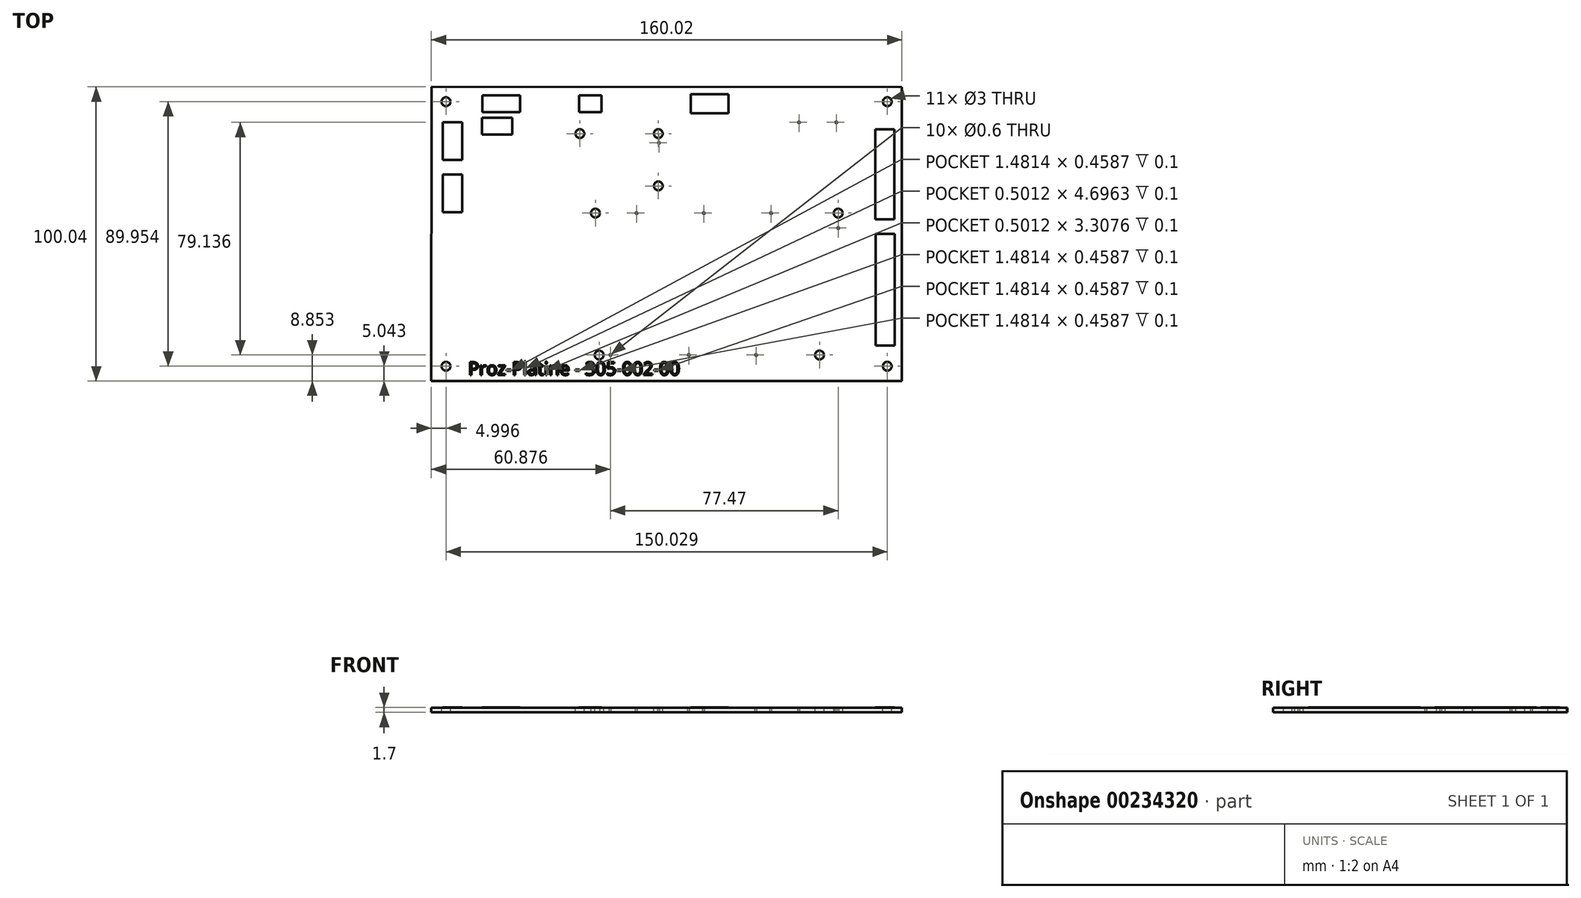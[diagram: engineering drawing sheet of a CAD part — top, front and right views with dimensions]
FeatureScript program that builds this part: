
annotation { "Feature Type Name" : "Feature", "Feature Type Description" : "" }
export const myFeature = defineFeature(function(context is Context, id is Id, definition is map)
    precondition{}
    {
        {
            var Q0;
            Q0=qCreatedBy(makeId("Top.planeOp"),FACE);
            var sketch = newSketch(context, id + "F0", { "sketchPlane" : qUnion([Q0])});
            skLineSegment(sketch, "E0.bottom", {"start": v(79.99, -50.02) * mm, "end": v(-80.01, -49.98) * mm});
            skLineSegment(sketch, "E0.top", {"start": v(80.01, 49.98) * mm, "end": v(-79.99, 50.02) * mm});
            skLineSegment(sketch, "E0.left", {"start": v(79.99, -50.02) * mm, "end": v(80.01, 49.98) * mm});
            skLineSegment(sketch, "E0.right", {"start": v(-80.01, -49.98) * mm, "end": v(-79.99, 50.02) * mm});
            skPoint(sketch, "E0.middle", {"position": v(0, 0) * mm});
            skCircle(sketch, "E1", {"center": v(-75.01, -44.98) * mm, "radius": 1.5 * mm});
            skCircle(sketch, "E2.MirrorC", {"center": v(75.01, -44.98) * mm, "radius": 1.5 * mm});
            skCircle(sketch, "E3.MirrorC", {"center": v(-75.01, 44.98) * mm, "radius": 1.5 * mm});
            skCircle(sketch, "E4.MirrorC", {"center": v(75.01, 44.98) * mm, "radius": 1.5 * mm});
            skCircle(sketch, "E5", {"center": v(-22.94, -41.17) * mm, "radius": 1.5 * mm});
            skCircle(sketch, "E6", {"center": v(-24.21, 7.1) * mm, "radius": 1.5 * mm});
            skCircle(sketch, "E7", {"center": v(58.34, 7.1) * mm, "radius": 1.5 * mm});
            skCircle(sketch, "E8", {"center": v(51.99, -41.17) * mm, "radius": 1.5 * mm});
            skCircle(sketch, "E9", {"center": v(-29.5, 34.12) * mm, "radius": 1.5 * mm});
            skCircle(sketch, "E10", {"center": v(-2.83, 34.12) * mm, "radius": 1.5 * mm});
            skCircle(sketch, "E11", {"center": v(-2.83, 16.34) * mm, "radius": 1.5 * mm});
            skCircle(sketch, "E12", {"center": v(-19.13, -41.17) * mm, "radius": 0.3 * mm});
            skCircle(sketch, "E13", {"center": v(7.54, -41.17) * mm, "radius": 0.3 * mm});
            skCircle(sketch, "E14", {"center": v(30.4, -41.17) * mm, "radius": 0.3 * mm});
            skCircle(sketch, "E15", {"center": v(58.34, 2.01) * mm, "radius": 0.3 * mm});
            skCircle(sketch, "E16", {"center": v(-10.24, 7.1) * mm, "radius": 0.3 * mm});
            skCircle(sketch, "E17", {"center": v(12.62, 7.1) * mm, "radius": 0.3 * mm});
            skCircle(sketch, "E18", {"center": v(35.48, 7.1) * mm, "radius": 0.3 * mm});
            skCircle(sketch, "E19", {"center": v(57.7, 37.97) * mm, "radius": 0.3 * mm});
            skCircle(sketch, "E20", {"center": v(45, 37.97) * mm, "radius": 0.3 * mm});
            skCircle(sketch, "E21", {"center": v(-2.62, 31) * mm, "radius": 0.3 * mm});
            skLineSegment(sketch, "E22.bottom", {"start": v(-69.58, 25.22) * mm, "end": v(-76.08, 25.22) * mm});
            skLineSegment(sketch, "E22.top", {"start": v(-69.58, 38.02) * mm, "end": v(-76.08, 38.02) * mm});
            skLineSegment(sketch, "E22.left", {"start": v(-69.58, 25.22) * mm, "end": v(-69.58, 38.02) * mm});
            skLineSegment(sketch, "E22.right", {"start": v(-76.08, 25.22) * mm, "end": v(-76.08, 38.02) * mm});
            skPoint(sketch, "E22.middle", {"position": v(-72.83, 31.62) * mm});
            skLineSegment(sketch, "E23.bottom", {"start": v(-69.58, 7.44) * mm, "end": v(-76.08, 7.44) * mm});
            skLineSegment(sketch, "E23.top", {"start": v(-69.58, 20.24) * mm, "end": v(-76.08, 20.24) * mm});
            skLineSegment(sketch, "E23.left", {"start": v(-69.58, 7.44) * mm, "end": v(-69.58, 20.24) * mm});
            skLineSegment(sketch, "E23.right", {"start": v(-76.08, 7.44) * mm, "end": v(-76.08, 20.24) * mm});
            skPoint(sketch, "E23.middle", {"position": v(-72.83, 13.84) * mm});
            skLineSegment(sketch, "E24.bottom", {"start": v(21, 41.05) * mm, "end": v(8.2, 41.05) * mm});
            skLineSegment(sketch, "E24.top", {"start": v(21, 47.55) * mm, "end": v(8.2, 47.55) * mm});
            skLineSegment(sketch, "E24.left", {"start": v(21, 41.05) * mm, "end": v(21, 47.55) * mm});
            skLineSegment(sketch, "E24.right", {"start": v(8.2, 41.05) * mm, "end": v(8.2, 47.55) * mm});
            skPoint(sketch, "E24.middle", {"position": v(14.6, 44.3) * mm});
            skLineSegment(sketch, "E25.bottom", {"start": v(77.39, 4.99) * mm, "end": v(70.89, 4.99) * mm});
            skLineSegment(sketch, "E25.top", {"start": v(77.39, 35.59) * mm, "end": v(70.89, 35.59) * mm});
            skLineSegment(sketch, "E25.left", {"start": v(77.39, 4.99) * mm, "end": v(77.39, 35.59) * mm});
            skLineSegment(sketch, "E25.right", {"start": v(70.89, 4.99) * mm, "end": v(70.89, 35.59) * mm});
            skPoint(sketch, "E25.middle", {"position": v(74.14, 20.29) * mm});
            skLineSegment(sketch, "E26.bottom", {"start": v(77.56, -37.95) * mm, "end": v(71.06, -37.95) * mm});
            skLineSegment(sketch, "E26.top", {"start": v(77.56, 0.05) * mm, "end": v(71.06, 0.05) * mm});
            skLineSegment(sketch, "E26.left", {"start": v(77.56, -37.95) * mm, "end": v(77.56, 0.05) * mm});
            skLineSegment(sketch, "E26.right", {"start": v(71.06, -37.95) * mm, "end": v(71.06, 0.05) * mm});
            skPoint(sketch, "E26.middle", {"position": v(74.3, -18.95) * mm});
            skLineSegment(sketch, "E27.bottom", {"start": v(-49.9, 41.47) * mm, "end": v(-62.7, 41.47) * mm});
            skLineSegment(sketch, "E27.top", {"start": v(-49.9, 47.17) * mm, "end": v(-62.7, 47.17) * mm});
            skLineSegment(sketch, "E27.left", {"start": v(-49.9, 41.47) * mm, "end": v(-49.9, 47.17) * mm});
            skLineSegment(sketch, "E27.right", {"start": v(-62.7, 41.47) * mm, "end": v(-62.7, 47.17) * mm});
            skPoint(sketch, "E27.middle", {"position": v(-56.3, 44.32) * mm});
            skLineSegment(sketch, "E28.bottom", {"start": v(-52.54, 33.86) * mm, "end": v(-62.84, 33.86) * mm});
            skLineSegment(sketch, "E28.top", {"start": v(-52.54, 39.56) * mm, "end": v(-62.84, 39.56) * mm});
            skLineSegment(sketch, "E28.left", {"start": v(-52.54, 33.86) * mm, "end": v(-52.54, 39.56) * mm});
            skLineSegment(sketch, "E28.right", {"start": v(-62.84, 33.86) * mm, "end": v(-62.84, 39.56) * mm});
            skPoint(sketch, "E28.middle", {"position": v(-57.7, 36.71) * mm});
            skLineSegment(sketch, "E29.bottom", {"start": v(-22.12, 41.4) * mm, "end": v(-29.72, 41.4) * mm});
            skLineSegment(sketch, "E29.top", {"start": v(-22.12, 47.1) * mm, "end": v(-29.72, 47.1) * mm});
            skLineSegment(sketch, "E29.left", {"start": v(-22.12, 41.4) * mm, "end": v(-22.12, 47.1) * mm});
            skLineSegment(sketch, "E29.right", {"start": v(-29.72, 41.4) * mm, "end": v(-29.72, 47.1) * mm});
            skPoint(sketch, "E29.middle", {"position": v(-25.92, 44.26) * mm});
            skSolve(sketch);
        }
        {
            var Q0;
            Q0=makeQuery(id+"F0.imprint","IMPRINT",FACE,{"disambiguationData":[TD([[makeQuery(id+"F0.imprint","IMPRINT",EDGE,{"derivedFrom":sQuery(id+"F0.wireOp",EDGE,"E0.bottom")}),-1.0]])]});
            var Q1;
            Q1=makeQuery(id+"F0.imprint","IMPRINT",FACE,{"disambiguationData":[TD([[makeQuery(id+"F0.imprint","IMPRINT",EDGE,{"derivedFrom":sQuery(id+"F0.wireOp",EDGE,"E23.bottom")}),-1.0]])]});
            var Q2;
            Q2=makeQuery(id+"F0.imprint","IMPRINT",FACE,{"disambiguationData":[TD([[makeQuery(id+"F0.imprint","IMPRINT",EDGE,{"derivedFrom":sQuery(id+"F0.wireOp",EDGE,"E22.bottom")}),-1.0]])]});
            var Q3;
            Q3=makeQuery(id+"F0.imprint","IMPRINT",FACE,{"disambiguationData":[TD([[makeQuery(id+"F0.imprint","IMPRINT",EDGE,{"derivedFrom":sQuery(id+"F0.wireOp",EDGE,"E28.bottom")}),-1.0]])]});
            var Q4;
            Q4=makeQuery(id+"F0.imprint","IMPRINT",FACE,{"disambiguationData":[TD([[makeQuery(id+"F0.imprint","IMPRINT",EDGE,{"derivedFrom":sQuery(id+"F0.wireOp",EDGE,"E27.bottom")}),-1.0]])]});
            var Q5;
            Q5=makeQuery(id+"F0.imprint","IMPRINT",FACE,{"disambiguationData":[TD([[makeQuery(id+"F0.imprint","IMPRINT",EDGE,{"derivedFrom":sQuery(id+"F0.wireOp",EDGE,"E29.bottom")}),-1.0]])]});
            var Q6;
            Q6=makeQuery(id+"F0.imprint","IMPRINT",FACE,{"disambiguationData":[TD([[makeQuery(id+"F0.imprint","IMPRINT",EDGE,{"derivedFrom":sQuery(id+"F0.wireOp",EDGE,"E24.bottom")}),-1.0]])]});
            var Q7;
            Q7=makeQuery(id+"F0.imprint","IMPRINT",FACE,{"disambiguationData":[TD([[makeQuery(id+"F0.imprint","IMPRINT",EDGE,{"derivedFrom":sQuery(id+"F0.wireOp",EDGE,"E25.bottom")}),-1.0]])]});
            var Q8;
            Q8=makeQuery(id+"F0.imprint","IMPRINT",FACE,{"disambiguationData":[TD([[makeQuery(id+"F0.imprint","IMPRINT",EDGE,{"derivedFrom":sQuery(id+"F0.wireOp",EDGE,"E26.bottom")}),-1.0]])]});
            extrude(context, id + "F1", {"entities" : qUnion([Q0, Q1, Q2, Q3, Q4, Q5, Q6, Q7, Q8]), "oppositeDirection" : true, "offsetDistance" : 25 * mm, "depth" : 1.6 * mm});
        }
        {
            var Q0;
            Q0=makeQuery(id+"F1.opExtrude","CAP_FACE",FACE,{"disambiguationData":[OSD([sQuery(id+"F0.wireOp",EDGE,"E0.bottom"),sQuery(id+"F0.wireOp",EDGE,"E0.top"),sQuery(id+"F0.wireOp",EDGE,"E0.left"),sQuery(id+"F0.wireOp",EDGE,"E0.right"),sQuery(id+"F0.wireOp",EDGE,"E1"),sQuery(id+"F0.wireOp",EDGE,"E2.MirrorC")])],"isStart":true});
            var sketch = newSketch(context, id + "F2", { "sketchPlane" : qUnion([Q0])});
            skText(sketch, "E30", { "text": "Proz-Platine - 305-002-00", "fontName": "OpenSans-Regular.ttf"});
            const initialGuessF2  = {"E30": [-0.06752, -0.04799, 1, 0, 0.00445]};
            skSetInitialGuess(sketch, initialGuessF2);
            skSolve(sketch);
        }
        {
            var Q0;
            Q0=qSketchRegion(id+"F2",true);
            extrude(context, id + "F3", {"entities" : qUnion([Q0]), "operationType" : NewBodyOperationType.REMOVE, "oppositeDirection" : true, "depth" : .1 * mm});
        }
        {
            var Q0;
            Q0=makeQuery(id+"F0.imprint","IMPRINT",FACE,{"disambiguationData":[TD([[makeQuery(id+"F0.imprint","IMPRINT",EDGE,{"derivedFrom":sQuery(id+"F0.wireOp",EDGE,"E23.bottom")}),-1.0]])]});
            var Q1;
            Q1=makeQuery(id+"F0.imprint","IMPRINT",FACE,{"disambiguationData":[TD([[makeQuery(id+"F0.imprint","IMPRINT",EDGE,{"derivedFrom":sQuery(id+"F0.wireOp",EDGE,"E22.bottom")}),-1.0]])]});
            var Q2;
            Q2=makeQuery(id+"F0.imprint","IMPRINT",FACE,{"disambiguationData":[TD([[makeQuery(id+"F0.imprint","IMPRINT",EDGE,{"derivedFrom":sQuery(id+"F0.wireOp",EDGE,"E28.bottom")}),-1.0]])]});
            var Q3;
            Q3=makeQuery(id+"F0.imprint","IMPRINT",FACE,{"disambiguationData":[TD([[makeQuery(id+"F0.imprint","IMPRINT",EDGE,{"derivedFrom":sQuery(id+"F0.wireOp",EDGE,"E27.bottom")}),-1.0]])]});
            var Q4;
            Q4=makeQuery(id+"F0.imprint","IMPRINT",FACE,{"disambiguationData":[TD([[makeQuery(id+"F0.imprint","IMPRINT",EDGE,{"derivedFrom":sQuery(id+"F0.wireOp",EDGE,"E29.bottom")}),-1.0]])]});
            var Q5;
            Q5=makeQuery(id+"F0.imprint","IMPRINT",FACE,{"disambiguationData":[TD([[makeQuery(id+"F0.imprint","IMPRINT",EDGE,{"derivedFrom":sQuery(id+"F0.wireOp",EDGE,"E24.bottom")}),-1.0]])]});
            var Q6;
            Q6=makeQuery(id+"F0.imprint","IMPRINT",FACE,{"disambiguationData":[TD([[makeQuery(id+"F0.imprint","IMPRINT",EDGE,{"derivedFrom":sQuery(id+"F0.wireOp",EDGE,"E25.bottom")}),-1.0]])]});
            var Q7;
            Q7=makeQuery(id+"F0.imprint","IMPRINT",FACE,{"disambiguationData":[TD([[makeQuery(id+"F0.imprint","IMPRINT",EDGE,{"derivedFrom":sQuery(id+"F0.wireOp",EDGE,"E26.bottom")}),-1.0]])]});
            extrude(context, id + "F4", {"entities" : qUnion([Q0, Q1, Q2, Q3, Q4, Q5, Q6, Q7]), "operationType" : NewBodyOperationType.ADD, "depth" : .1 * mm, "offsetDistance" : 25 * mm});
        }
    });
